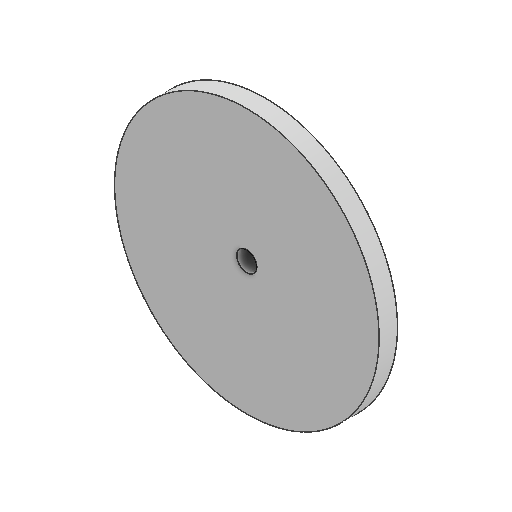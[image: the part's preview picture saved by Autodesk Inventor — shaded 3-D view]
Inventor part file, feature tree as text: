
AUTODESK INVENTOR PART (.ipt)
format: ipt  version: 2025.2 (Build 292293000, 293)  size: 85,504 bytes
history: native  units: in
note: dims shown in document units (in); Inventor stores cm internally (conversion verified against a paired STEP export)
features: extrude x1, sketch x1
ambient origin geometry x8: Origin, YZ Plane, XZ Plane, XY Plane, X Axis, Y Axis, Z Axis, Center Point
bodies: Solid1 (feature_tree)
feature tree (2):
  extrude  "Extrusion1"  Depth=0.4331in
  sketch  "Sketch1"  dims[d0=0.4724in d1=6.2323in d2=0.4331in d3=0.0in]
